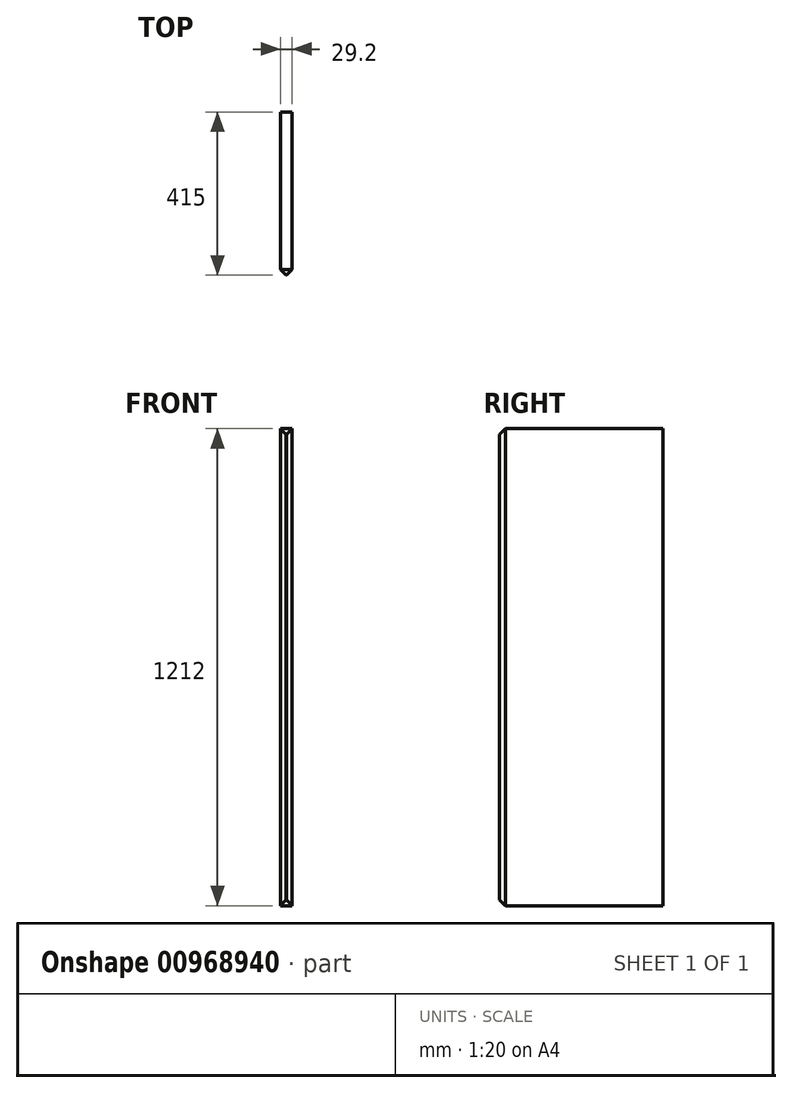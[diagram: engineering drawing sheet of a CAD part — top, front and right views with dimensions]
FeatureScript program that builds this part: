
annotation { "Feature Type Name" : "Feature", "Feature Type Description" : "" }
export const myFeature = defineFeature(function(context is Context, id is Id, definition is map)
    precondition{}
    {
        {
            var Q0;
            Q0=qCreatedBy(makeId("Front.planeOp"),FACE);
            var sketch = newSketch(context, id + "F0", { "sketchPlane" : qUnion([Q0])});
            skLineSegment(sketch, "E0.bottom", {"start": v(405, -875) * mm, "end": v(-405, -875) * mm});
            skLineSegment(sketch, "E0.top", {"start": v(405, 875) * mm, "end": v(-405, 875) * mm});
            skLineSegment(sketch, "E0.left", {"start": v(405, -875) * mm, "end": v(405, 875) * mm});
            skLineSegment(sketch, "E0.right", {"start": v(-405, -875) * mm, "end": v(-405, 875) * mm});
            skPoint(sketch, "E0.middle", {"position": v(0, 0) * mm});
            skLineSegment(sketch, "E1.bottom", {"start": v(-379.6, 828) * mm, "end": v(379.6, 828) * mm});
            skLineSegment(sketch, "E1.top", {"start": v(-379.6, -827) * mm, "end": v(379.6, -827) * mm});
            skLineSegment(sketch, "E1.left", {"start": v(-379.6, 828) * mm, "end": v(-379.6, -827) * mm});
            skLineSegment(sketch, "E1.right", {"start": v(379.6, 828) * mm, "end": v(379.6, -827) * mm});
            skLineSegment(sketch, "E2", {"start": v(-359.6, 385) * mm, "end": v(379.6, 385) * mm});
            skLineSegment(sketch, "E3", {"start": v(379.6, 410) * mm, "end": v(-359.6, 410) * mm});
            skLineSegment(sketch, "E4", {"start": v(-359.6, 828) * mm, "end": v(-359.6, -827) * mm});
            skLineSegment(sketch, "E5", {"start": v(-4.6, 385) * mm, "end": v(-4.6, -827) * mm});
            skLineSegment(sketch, "E6", {"start": v(24.6, 385) * mm, "end": v(24.6, -827) * mm});
            skLineSegment(sketch, "E7", {"start": v(-359.6, 25) * mm, "end": v(-4.6, 25) * mm});
            skLineSegment(sketch, "E8", {"start": v(-359.6, 10) * mm, "end": v(-4.6, 10) * mm});
            skLineSegment(sketch, "E9.0.1.0", {"start": v(-359.6, -350) * mm, "end": v(-4.6, -350) * mm});
            skLineSegment(sketch, "E9.0.1.1", {"start": v(-359.6, -365) * mm, "end": v(-4.6, -365) * mm});
            skLineSegment(sketch, "E9.0.2.0", {"start": v(-359.6, -725) * mm, "end": v(-4.6, -725) * mm});
            skLineSegment(sketch, "E9.0.2.1", {"start": v(-359.6, -740) * mm, "end": v(-4.6, -740) * mm});
            skLineSegment(sketch, "E9.1.0.0", {"start": v(24.6, 25) * mm, "end": v(379.6, 25) * mm});
            skLineSegment(sketch, "E9.1.0.1", {"start": v(24.6, 10) * mm, "end": v(379.6, 10) * mm});
            skLineSegment(sketch, "E9.1.1.0", {"start": v(24.6, -350) * mm, "end": v(379.6, -350) * mm});
            skLineSegment(sketch, "E9.1.1.1", {"start": v(24.6, -365) * mm, "end": v(379.6, -365) * mm});
            skLineSegment(sketch, "E9.1.2.0", {"start": v(24.6, -725) * mm, "end": v(379.6, -725) * mm});
            skLineSegment(sketch, "E9.1.2.1", {"start": v(24.6, -740) * mm, "end": v(379.6, -740) * mm});
            skLineSegment(sketch, "E9.direction1", {"start": v(-359.6, 25) * mm, "end": v(24.6, 25) * mm, "construction": true});
            skLineSegment(sketch, "E9.direction2", {"start": v(-359.6, 25) * mm, "end": v(-359.6, -350) * mm, "construction": true});
            skSolve(sketch);
        }
        {
            var Q0;
            {var subQ4=sQuery(id+"F0.wireOp",EDGE,"E5");var subQ5=sQuery(id+"F0.wireOp",EDGE,"E1.top");var subQ6=makeQuery(id+"F0.imprint","INTERSECT",VERTEX,{"derivedFrom":[subQ5,subQ4]});Q0=makeQuery(id+"F0.imprint","IMPRINT",FACE,{"disambiguationData":[TD([[makeQuery(id+"F0.imprint","IMPRINT",EDGE,{"disambiguationData":[TD([[subQ6,-1.0]])],"derivedFrom":subQ5}),1.0]])]});}
            extrude(context, id + "F1", {"entities" : qUnion([Q0]), "oppositeDirection" : true, "depth" : 470 * mm, "offsetDistance" : 25 * mm, "hasSecondDirection" : true, "secondDirectionOppositeDirection" : true, "secondDirectionDepth" : 55 * mm});
        }
        {
            var Q0;
            Q0=makeQuery(id+"F1.opExtrude","CAP_FACE",FACE,{"disambiguationData":[OSD([sQuery(id+"F0.wireOp",EDGE,"E1.top"),sQuery(id+"F0.wireOp",EDGE,"E2"),sQuery(id+"F0.wireOp",EDGE,"E5"),sQuery(id+"F0.wireOp",EDGE,"E6")])],"isStart":true});
            chamfer(context, id + "F2", {"entities" : qUnion([Q0]), "chamferType" : ChamferType.OFFSET_ANGLE, "width" : 14.5 * mm, "oppositeDirection" : false, "angle" : 45 * degree, "tangentPropagation" : true});
        }
    });
